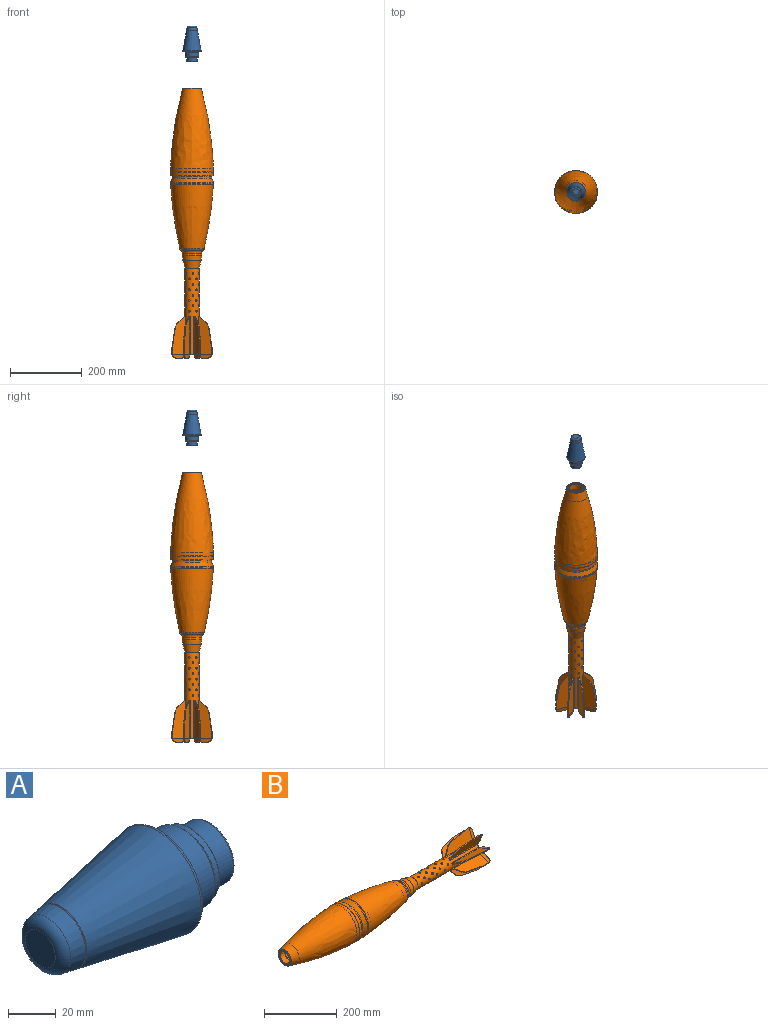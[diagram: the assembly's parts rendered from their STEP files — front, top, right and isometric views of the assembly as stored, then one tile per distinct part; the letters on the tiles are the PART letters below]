
ASSEMBLY  parts=2 mates=1
PART A: 17 faces, bbox 100x50.8x50.8 mm
  f0: torus R=13.88mm, axis (-1,0,0), area 149.5mm2, adj f1,f14
  f1: plane 27.76x27.76mm, normal (1,0,0), area 605.3mm2, adj f0
  f2: plane 17.63x17.63mm, normal (-1,0,0), area 244.1mm2, adj f16
  f3: cone r=13mm half-angle=10.1deg, axis (1,0,0), area 702.8mm2, adj f4,f16
  f4: torus R=15.15mm, axis (-1,0,0), area 74mm2, adj f3,f5
  f5: cone r=15.19mm half-angle=10.1deg, axis (1,0,0), area 7404mm2, adj f4,f6
  f6: cylinder r=25.42mm len=50.83mm, axis (-1,0,0), area 149.7mm2, adj f5,f7
  f7: plane 50.83x50.83mm, normal (1,0,0), area 1044.3mm2, adj f6,f8
  f8: cylinder r=17.71mm len=35.42mm, axis (-1,0,0), area 266.6mm2, adj f7,f9
  f9: cone r=17.71mm half-angle=45deg, axis (1,0,0), area 248.7mm2, adj f8,f10
  f10: cylinder r=19.22mm len=38.45mm, axis (-1,0,0), area 1168.9mm2, adj f9,f11
  f11: cone r=19.22mm half-angle=45deg, axis (-1,0,0), area 248.7mm2, adj f10,f12
  f12: cylinder r=17.71mm len=35.42mm, axis (-1,0,0), area 292.1mm2, adj f11,f15
  f13: plane 34.42x34.42mm, normal (1,0,0), area 230.8mm2, adj f14,f15
  f14: cylinder r=14.92mm len=29.84mm, axis (-1,0,0), area 976.6mm2, adj f0,f13
  f15: cone r=17.71mm half-angle=45deg, axis (-1,0,0), area 77.6mm2, adj f12,f13
  f16: torus R=8.82mm, axis (-1,0,0), area 515.4mm2, adj f2,f3
PART B: 246 faces, bbox 750x124.9x124.9 mm
  f0: plane 119.06x119.06mm, normal (1,0,0), area 70.5mm2, adj f3,f17
  f1: cone r=59.71mm half-angle=19.9deg, axis (1,0,0), area 4983.2mm2, adj f2,f6
  f2: cylinder r=59.71mm len=119.42mm, axis (-1,0,0), area 750.4mm2, adj f1,f3
  f3: revolved ~119.42x119.42mm, area 1125.9mm2, adj f0,f2
  f4: cylinder r=59.71mm len=119.42mm, axis (-1,0,0), area 3376.6mm2, adj f8,f9
  f5: plane 118.42x118.42mm, normal (1,0,0), area 1162.6mm2, adj f7,f9
  f6: cylinder r=55mm len=110mm, axis (-1,0,0), area 2073.5mm2, adj f1,f7
  f7: torus R=56mm, axis (-1,0,0), area 546.4mm2, adj f5,f6
  f8: cone r=59.21mm half-angle=45deg, axis (1,0,0), area 264.2mm2, adj f4,f203
  f9: cone r=59.71mm half-angle=45deg, axis (-1,0,0), area 264.2mm2, adj f4,f5
  f10: cone r=20mm half-angle=14deg, axis (-1,0,0), area 3215.5mm2, adj f11,f85
  f11: revolved ~54.46x54.46mm, area 2453.5mm2, adj f10,f12
  f12: cylinder r=27.23mm len=54.46mm, axis (-1,0,0), area 939.4mm2, adj f11,f13
  f13: torus R=37.23mm, axis (-1,0,0), area 1393mm2, adj f12,f14
  f14: cone r=30.16mm half-angle=45deg, axis (-1,0,0), area 331.2mm2, adj f13,f15
  f15: torus R=24.3mm, axis (-1,0,0), area 1161.1mm2, adj f14,f16
  f16: revolved ~176.81x119.04mm, area 55262.1mm2, adj f15,f17
  f17: cone r=59.34mm half-angle=41.5deg, axis (1,0,0), area 99.5mm2, adj f0,f16
  f18: plane 37.6x15.64mm, normal (0.1,0.38,-0.92), area 365.6mm2, adj f84,f86,f87,f88,f89
  f19: plane 37.6x15.64mm, normal (0.1,-0.38,0.92), area 365.6mm2, adj f84,f86,f87,f88,f90
  f20: cylinder r=30mm len=4.98mm, axis (0,0.38,-0.92), area 15mm2, adj f27,f28,f89,f90
  f21: cylinder r=30mm len=18.62mm, axis (0,0.38,-0.92), area 66.5mm2, adj f26,f27,f89,f90
  f22: cylinder r=2mm len=106.15mm, axis (1,0,0), area 298.3mm2, adj f24,f25,f26,f84,f85,f89
  f23: cylinder r=2mm len=106.15mm, axis (1,0,0), area 298.3mm2, adj f24,f25,f26,f84,f85,f90
  f24: plane 5.88x2.45mm, normal (-1,0,0), area 1mm2, adj f22,f23,f25,f85
  f25: plane 4.18x1.73mm, normal (0,0.92,0.38), area 0.7mm2, adj f22,f23,f24,f26
  f26: plane 19.65x15.46mm, normal (-0.79,0.57,0.24), area 76.1mm2, adj f21,f22,f23,f25,f89,f90
  f27: plane 49.44x8.84mm, normal (-0.17,0.91,0.38), area 150.4mm2, adj f20,f21,f89,f90
  f28: plane 17.49x2.77mm, normal (0,0.92,0.38), area 52.5mm2, adj f20,f86,f89,f90
  f29: cylinder r=2.62mm len=11mm, axis (0,-0.61,-0.79), area 158mm2, adj f83,f85
  f30: cylinder r=2.62mm len=11.09mm, axis (0,0.38,-0.92), area 158mm2, adj f83,f85
  f31: cylinder r=2.62mm len=10.44mm, axis (0,0.99,-0.13), area 158mm2, adj f83,f85
  f32: cylinder r=2.62mm len=11mm, axis (0,0.61,0.79), area 158mm2, adj f83,f85
  f33: cylinder r=2.62mm len=10.44mm, axis (0,-0.99,0.13), area 158mm2, adj f83,f85
  f34: cylinder r=2.62mm len=11mm, axis (0,-0.61,-0.79), area 158mm2, adj f83,f85
  f35: cylinder r=2.62mm len=11.09mm, axis (0,0.38,-0.92), area 158mm2, adj f83,f85
  f36: cylinder r=2.62mm len=10.44mm, axis (0,0.99,-0.13), area 158mm2, adj f83,f85
  f37: cylinder r=2.62mm len=11mm, axis (0,0.61,0.79), area 158mm2, adj f83,f85
  f38: cylinder r=2.62mm len=10.44mm, axis (0,-0.99,0.13), area 158mm2, adj f83,f85
  f39: cylinder r=2.62mm len=11mm, axis (0,-0.61,-0.79), area 158mm2, adj f83,f85
  f40: cylinder r=2.62mm len=11.09mm, axis (0,0.38,-0.92), area 158mm2, adj f83,f85
  f41: cylinder r=2.62mm len=10.44mm, axis (0,0.99,-0.13), area 158mm2, adj f83,f85
  f42: cylinder r=2.62mm len=11mm, axis (0,0.61,0.79), area 158mm2, adj f83,f85
  f43: cylinder r=2.62mm len=10.44mm, axis (0,-0.99,0.13), area 158mm2, adj f83,f85
  f44: cylinder r=2.62mm len=11mm, axis (0,-0.61,-0.79), area 158mm2, adj f83,f85
  f45: cylinder r=2.62mm len=11.09mm, axis (0,0.38,-0.92), area 158mm2, adj f83,f85
  f46: cylinder r=2.62mm len=10.44mm, axis (0,0.99,-0.13), area 158mm2, adj f83,f85
  f47: cylinder r=2.62mm len=11mm, axis (0,0.61,0.79), area 158mm2, adj f83,f85
  f48: cylinder r=2.62mm len=10.44mm, axis (0,-0.99,0.13), area 158mm2, adj f83,f85
  f49: cylinder r=2.62mm len=11.09mm, axis (0,-0.38,0.92), area 158mm2, adj f83,f85
  f50: cylinder r=2.62mm len=11.09mm, axis (0,-0.38,0.92), area 158mm2, adj f83,f85
  f51: cylinder r=2.62mm len=11.09mm, axis (0,-0.38,0.92), area 158mm2, adj f83,f85
  f52: cylinder r=2.62mm len=11.09mm, axis (0,-0.38,0.92), area 158mm2, adj f83,f85
  f53: cylinder r=2.62mm len=11mm, axis (0,0.79,-0.61), area 158mm2, adj f83,f85
  f54: cylinder r=2.62mm len=11.09mm, axis (0,0.92,0.38), area 158mm2, adj f83,f85
  f55: cylinder r=2.62mm len=10.44mm, axis (0,0.13,0.99), area 158mm2, adj f83,f85
  f56: cylinder r=2.62mm len=11mm, axis (0,-0.79,0.61), area 158mm2, adj f83,f85
  f57: cylinder r=2.62mm len=10.44mm, axis (0,-0.13,-0.99), area 158mm2, adj f83,f85
  f58: cylinder r=2.62mm len=11mm, axis (0,0.79,-0.61), area 158mm2, adj f83,f85
  f59: cylinder r=2.62mm len=11.09mm, axis (0,0.92,0.38), area 158mm2, adj f83,f85
  f60: cylinder r=2.62mm len=10.44mm, axis (0,0.13,0.99), area 158mm2, adj f83,f85
  f61: cylinder r=2.62mm len=11mm, axis (0,-0.79,0.61), area 158mm2, adj f83,f85
  f62: cylinder r=2.62mm len=10.44mm, axis (0,-0.13,-0.99), area 158mm2, adj f83,f85
  f63: cylinder r=2.62mm len=11mm, axis (0,0.79,-0.61), area 158mm2, adj f83,f85
  f64: cylinder r=2.62mm len=11.09mm, axis (0,0.92,0.38), area 158mm2, adj f83,f85
  f65: cylinder r=2.62mm len=10.44mm, axis (0,0.13,0.99), area 158mm2, adj f83,f85
  f66: cylinder r=2.62mm len=11mm, axis (0,-0.79,0.61), area 158mm2, adj f83,f85
  f67: cylinder r=2.62mm len=10.44mm, axis (0,-0.13,-0.99), area 158mm2, adj f83,f85
  f68: cylinder r=2.62mm len=11mm, axis (0,0.79,-0.61), area 158mm2, adj f83,f85
  f69: cylinder r=2.62mm len=11.09mm, axis (0,0.92,0.38), area 158mm2, adj f83,f85
  f70: cylinder r=2.62mm len=10.44mm, axis (0,0.13,0.99), area 158mm2, adj f83,f85
  f71: cylinder r=2.62mm len=11mm, axis (0,-0.79,0.61), area 158mm2, adj f83,f85
  f72: cylinder r=2.62mm len=10.44mm, axis (0,-0.13,-0.99), area 158mm2, adj f83,f85
  f73: cylinder r=2.62mm len=11.09mm, axis (0,-0.92,-0.38), area 158mm2, adj f83,f85
  f74: cylinder r=2.62mm len=11.09mm, axis (0,-0.92,-0.38), area 158mm2, adj f83,f85
  f75: cylinder r=2.62mm len=11.09mm, axis (0,-0.92,-0.38), area 158mm2, adj f83,f85
  f76: cylinder r=2.62mm len=11.09mm, axis (0,-0.92,-0.38), area 158mm2, adj f83,f85
  f77: plane 28x28mm, normal (1,0,0), area 149.3mm2, adj f78,f82
  f78: cone r=12.19mm half-angle=45deg, axis (1,0,0), area 103.8mm2, adj f77,f79
  f79: cylinder r=11.19mm len=23mm, axis (1,0,0), area 1616.4mm2, adj f78,f80
  f80: plane 22.37x22.37mm, normal (1,0,0), area 46.7mm2, adj f79,f83
  f81: plane 21x21mm, normal (1,0,0), area 346.4mm2, adj f83
  f82: cylinder r=14mm len=28mm, axis (1,0,0), area 263.9mm2, adj f77,f84
  f83: cylinder r=10.5mm len=203mm, axis (1,0,0), area 12346.6mm2, adj f29,f30,f31,f32,f33,f34,f35,f36
  f84: plane 41.29x41.29mm, normal (1,0,0), area 627.3mm2, adj f18,f19,f22,f23,f82,f85,f87,f99
  f85: cylinder r=20mm len=240mm, axis (1,0,0), area 23693.2mm2, adj f10,f22,f23,f24,f29,f30,f31,f32
  f86: cylinder r=10mm len=10.39mm, axis (0,0.38,-0.92), area 27.1mm2, adj f18,f19,f28,f88
  f87: cylinder r=10mm len=10.39mm, axis (0,0.38,-0.92), area 27.1mm2, adj f18,f19,f84,f88
  f88: plane 19.49x8.82mm, normal (1,0,0), area 20.7mm2, adj f18,f19,f86,f87
  f89: plane 104.77x35.08mm, normal (0,0.38,-0.92), area 3101.8mm2, adj f18,f20,f21,f22,f26,f27,f28
  f90: plane 104.77x35.08mm, normal (0,-0.38,0.92), area 3101.8mm2, adj f19,f20,f21,f23,f26,f27,f28
  f91: plane 104.77x35.05mm, normal (0,-0.92,0.38), area 3101.8mm2, adj f96,f97,f98,f100,f103,f104,f106
  f92: plane 104.77x35.05mm, normal (0,0.92,-0.38), area 3101.8mm2, adj f96,f97,f98,f99,f103,f104,f105
  f93: plane 19.48x8.85mm, normal (1,0,0), area 20.7mm2, adj f101,f102,f105,f106
  f94: plane 5.88x2.46mm, normal (-1,0,0), area 1mm2, adj f85,f95,f99,f100
  f95: plane 4.18x1.73mm, normal (0,0.38,0.92), area 0.7mm2, adj f94,f96,f99,f100
  f96: plane 19.65x15.46mm, normal (-0.79,0.24,0.57), area 76.1mm2, adj f91,f92,f95,f99,f100,f103
  f97: plane 49.44x8.84mm, normal (-0.17,0.38,0.91), area 150.4mm2, adj f91,f92,f103,f104
  f98: plane 17.49x2.77mm, normal (0,0.38,0.92), area 52.5mm2, adj f91,f92,f102,f104
  f99: cylinder r=2mm len=106.15mm, axis (1,0,0), area 298.3mm2, adj f84,f85,f92,f94,f95,f96
  f100: cylinder r=2mm len=106.15mm, axis (1,0,0), area 298.3mm2, adj f84,f85,f91,f94,f95,f96
  f101: cylinder r=10mm len=10.39mm, axis (0,0.92,-0.38), area 27.1mm2, adj f84,f93,f105,f106
  f102: cylinder r=10mm len=10.39mm, axis (0,0.92,-0.38), area 27.1mm2, adj f93,f98,f105,f106
  f103: cylinder r=30mm len=18.62mm, axis (0,0.92,-0.38), area 66.5mm2, adj f91,f92,f96,f97
  f104: cylinder r=30mm len=4.98mm, axis (0,0.92,-0.38), area 15mm2, adj f91,f92,f97,f98
  f105: plane 37.57x15.71mm, normal (0.1,0.92,-0.38), area 365.6mm2, adj f84,f92,f93,f101,f102
  f106: plane 37.57x15.71mm, normal (0.1,-0.92,0.38), area 365.6mm2, adj f84,f91,f93,f101,f102
  f107: plane 104.77x35.08mm, normal (0,-0.92,-0.38), area 3101.8mm2, adj f112,f113,f114,f116,f119,f120,f122
  f108: plane 104.77x35.08mm, normal (0,0.92,0.38), area 3101.8mm2, adj f112,f113,f114,f115,f119,f120,f121
  f109: plane 19.49x8.82mm, normal (1,0,0), area 20.7mm2, adj f117,f118,f121,f122
  f110: plane 5.88x2.45mm, normal (-1,0,0), area 1mm2, adj f85,f111,f115,f116
  f111: plane 4.18x1.73mm, normal (0,-0.38,0.92), area 0.7mm2, adj f110,f112,f115,f116
  f112: plane 19.65x15.46mm, normal (-0.79,-0.24,0.57), area 76.1mm2, adj f107,f108,f111,f115,f116,f119
  f113: plane 49.44x8.84mm, normal (-0.17,-0.38,0.91), area 150.4mm2, adj f107,f108,f119,f120
  f114: plane 17.49x2.77mm, normal (0,-0.38,0.92), area 52.5mm2, adj f107,f108,f118,f120
  f115: cylinder r=2mm len=106.15mm, axis (1,0,0), area 298.3mm2, adj f84,f85,f108,f110,f111,f112
  f116: cylinder r=2mm len=106.15mm, axis (1,0,0), area 298.3mm2, adj f84,f85,f107,f110,f111,f112
  f117: cylinder r=10mm len=10.39mm, axis (0,0.92,0.38), area 27.1mm2, adj f84,f109,f121,f122
  f118: cylinder r=10mm len=10.39mm, axis (0,0.92,0.38), area 27.1mm2, adj f109,f114,f121,f122
  f119: cylinder r=30mm len=18.62mm, axis (0,0.92,0.38), area 66.5mm2, adj f107,f108,f112,f113
  f120: cylinder r=30mm len=4.98mm, axis (0,0.92,0.38), area 15mm2, adj f107,f108,f113,f114
  f121: plane 37.6x15.64mm, normal (0.1,0.92,0.38), area 365.6mm2, adj f84,f108,f109,f117,f118
  f122: plane 37.6x15.64mm, normal (0.1,-0.92,-0.38), area 365.6mm2, adj f84,f107,f109,f117,f118
  f123: plane 104.77x35.05mm, normal (0,-0.38,-0.92), area 3101.8mm2, adj f128,f129,f130,f132,f135,f136,f138
  f124: plane 104.77x35.05mm, normal (0,0.38,0.92), area 3101.8mm2, adj f128,f129,f130,f131,f135,f136,f137
  f125: plane 19.48x8.85mm, normal (1,0,0), area 20.7mm2, adj f133,f134,f137,f138
  f126: plane 5.88x2.46mm, normal (-1,0,0), area 1mm2, adj f85,f127,f131,f132
  f127: plane 4.18x1.73mm, normal (0,-0.92,0.38), area 0.7mm2, adj f126,f128,f131,f132
  f128: plane 19.65x15.46mm, normal (-0.79,-0.57,0.24), area 76.1mm2, adj f123,f124,f127,f131,f132,f135
  f129: plane 49.44x8.84mm, normal (-0.17,-0.91,0.38), area 150.4mm2, adj f123,f124,f135,f136
  f130: plane 17.49x2.77mm, normal (0,-0.92,0.38), area 52.5mm2, adj f123,f124,f134,f136
  f131: cylinder r=2mm len=106.15mm, axis (1,0,0), area 298.3mm2, adj f84,f85,f124,f126,f127,f128
  f132: cylinder r=2mm len=106.15mm, axis (1,0,0), area 298.3mm2, adj f84,f85,f123,f126,f127,f128
  f133: cylinder r=10mm len=10.39mm, axis (0,0.38,0.92), area 27.1mm2, adj f84,f125,f137,f138
  f134: cylinder r=10mm len=10.39mm, axis (0,0.38,0.92), area 27.1mm2, adj f125,f130,f137,f138
  f135: cylinder r=30mm len=18.62mm, axis (0,0.38,0.92), area 66.5mm2, adj f123,f124,f128,f129
  f136: cylinder r=30mm len=4.98mm, axis (0,0.38,0.92), area 15mm2, adj f123,f124,f129,f130
  f137: plane 37.57x15.71mm, normal (0.1,0.38,0.92), area 365.6mm2, adj f84,f124,f125,f133,f134
  f138: plane 37.57x15.71mm, normal (0.1,-0.38,-0.92), area 365.6mm2, adj f84,f123,f125,f133,f134
  f139: plane 104.77x35.08mm, normal (0,0.38,-0.92), area 3101.8mm2, adj f144,f145,f146,f148,f151,f152,f154
  f140: plane 104.77x35.08mm, normal (0,-0.38,0.92), area 3101.8mm2, adj f144,f145,f146,f147,f151,f152,f153
  f141: plane 19.49x8.82mm, normal (1,0,0), area 20.7mm2, adj f149,f150,f153,f154
  f142: plane 5.88x2.45mm, normal (-1,0,0), area 1mm2, adj f85,f143,f147,f148
  f143: plane 4.18x1.73mm, normal (0,-0.92,-0.38), area 0.7mm2, adj f142,f144,f147,f148
  f144: plane 19.65x15.46mm, normal (-0.79,-0.57,-0.24), area 76.1mm2, adj f139,f140,f143,f147,f148,f151
  f145: plane 49.44x8.84mm, normal (-0.17,-0.91,-0.38), area 150.4mm2, adj f139,f140,f151,f152
  f146: plane 17.49x2.77mm, normal (0,-0.92,-0.38), area 52.5mm2, adj f139,f140,f150,f152
  f147: cylinder r=2mm len=106.15mm, axis (1,0,0), area 298.3mm2, adj f84,f85,f140,f142,f143,f144
  f148: cylinder r=2mm len=106.15mm, axis (1,0,0), area 298.3mm2, adj f84,f85,f139,f142,f143,f144
  f149: cylinder r=10mm len=10.39mm, axis (0,-0.38,0.92), area 27.1mm2, adj f84,f141,f153,f154
  f150: cylinder r=10mm len=10.39mm, axis (0,-0.38,0.92), area 27.1mm2, adj f141,f146,f153,f154
  f151: cylinder r=30mm len=18.62mm, axis (0,-0.38,0.92), area 66.5mm2, adj f139,f140,f144,f145
  f152: cylinder r=30mm len=4.98mm, axis (0,-0.38,0.92), area 15mm2, adj f139,f140,f145,f146
  f153: plane 37.6x15.64mm, normal (0.1,-0.38,0.92), area 365.6mm2, adj f84,f140,f141,f149,f150
  f154: plane 37.6x15.64mm, normal (0.1,0.38,-0.92), area 365.6mm2, adj f84,f139,f141,f149,f150
  f155: plane 104.77x35.05mm, normal (0,0.92,-0.38), area 3101.8mm2, adj f160,f161,f162,f164,f167,f168,f170
  f156: plane 104.77x35.05mm, normal (0,-0.92,0.38), area 3101.8mm2, adj f160,f161,f162,f163,f167,f168,f169
  f157: plane 19.48x8.85mm, normal (1,0,0), area 20.7mm2, adj f165,f166,f169,f170
  f158: plane 5.88x2.46mm, normal (-1,0,0), area 1mm2, adj f85,f159,f163,f164
  f159: plane 4.18x1.73mm, normal (0,-0.38,-0.92), area 0.7mm2, adj f158,f160,f163,f164
  f160: plane 19.65x15.46mm, normal (-0.79,-0.24,-0.57), area 76.1mm2, adj f155,f156,f159,f163,f164,f167
  f161: plane 49.44x8.84mm, normal (-0.17,-0.38,-0.91), area 150.4mm2, adj f155,f156,f167,f168
  f162: plane 17.49x2.77mm, normal (0,-0.38,-0.92), area 52.5mm2, adj f155,f156,f166,f168
  f163: cylinder r=2mm len=106.15mm, axis (1,0,0), area 298.3mm2, adj f84,f85,f156,f158,f159,f160
  f164: cylinder r=2mm len=106.15mm, axis (1,0,0), area 298.3mm2, adj f84,f85,f155,f158,f159,f160
  f165: cylinder r=10mm len=10.39mm, axis (0,-0.92,0.38), area 27.1mm2, adj f84,f157,f169,f170
  f166: cylinder r=10mm len=10.39mm, axis (0,-0.92,0.38), area 27.1mm2, adj f157,f162,f169,f170
  f167: cylinder r=30mm len=18.62mm, axis (0,-0.92,0.38), area 66.5mm2, adj f155,f156,f160,f161
  f168: cylinder r=30mm len=4.98mm, axis (0,-0.92,0.38), area 15mm2, adj f155,f156,f161,f162
  f169: plane 37.57x15.71mm, normal (0.1,-0.92,0.38), area 365.6mm2, adj f84,f156,f157,f165,f166
  f170: plane 37.57x15.71mm, normal (0.1,0.92,-0.38), area 365.6mm2, adj f84,f155,f157,f165,f166
  f171: plane 104.77x35.08mm, normal (0,0.92,0.38), area 3101.8mm2, adj f176,f177,f178,f180,f183,f184,f186
  f172: plane 104.77x35.08mm, normal (0,-0.92,-0.38), area 3101.8mm2, adj f176,f177,f178,f179,f183,f184,f185
  f173: plane 19.49x8.82mm, normal (1,0,0), area 20.7mm2, adj f181,f182,f185,f186
  f174: plane 5.88x2.45mm, normal (-1,0,0), area 1mm2, adj f85,f175,f179,f180
  f175: plane 4.18x1.73mm, normal (0,0.38,-0.92), area 0.7mm2, adj f174,f176,f179,f180
  f176: plane 19.65x15.46mm, normal (-0.79,0.24,-0.57), area 76.1mm2, adj f171,f172,f175,f179,f180,f183
  f177: plane 49.44x8.84mm, normal (-0.17,0.38,-0.91), area 150.4mm2, adj f171,f172,f183,f184
  f178: plane 17.49x2.77mm, normal (0,0.38,-0.92), area 52.5mm2, adj f171,f172,f182,f184
  f179: cylinder r=2mm len=106.15mm, axis (1,0,0), area 298.3mm2, adj f84,f85,f172,f174,f175,f176
  f180: cylinder r=2mm len=106.15mm, axis (1,0,0), area 298.3mm2, adj f84,f85,f171,f174,f175,f176
  f181: cylinder r=10mm len=10.39mm, axis (0,-0.92,-0.38), area 27.1mm2, adj f84,f173,f185,f186
  f182: cylinder r=10mm len=10.39mm, axis (0,-0.92,-0.38), area 27.1mm2, adj f173,f178,f185,f186
  f183: cylinder r=30mm len=18.62mm, axis (0,-0.92,-0.38), area 66.5mm2, adj f171,f172,f176,f177
  f184: cylinder r=30mm len=4.98mm, axis (0,-0.92,-0.38), area 15mm2, adj f171,f172,f177,f178
  f185: plane 37.6x15.64mm, normal (0.1,-0.92,-0.38), area 365.6mm2, adj f84,f172,f173,f181,f182
  f186: plane 37.6x15.64mm, normal (0.1,0.92,0.38), area 365.6mm2, adj f84,f171,f173,f181,f182
  f187: plane 104.77x35.05mm, normal (0,0.38,0.92), area 3101.8mm2, adj f192,f193,f194,f196,f199,f200,f202
  f188: plane 104.77x35.05mm, normal (0,-0.38,-0.92), area 3101.8mm2, adj f192,f193,f194,f195,f199,f200,f201
  f189: plane 19.48x8.85mm, normal (1,0,0), area 20.7mm2, adj f197,f198,f201,f202
  f190: plane 5.88x2.46mm, normal (-1,0,0), area 1mm2, adj f85,f191,f195,f196
  f191: plane 4.18x1.73mm, normal (0,0.92,-0.38), area 0.7mm2, adj f190,f192,f195,f196
  f192: plane 19.65x15.46mm, normal (-0.79,0.57,-0.24), area 76.1mm2, adj f187,f188,f191,f195,f196,f199
  f193: plane 49.44x8.84mm, normal (-0.17,0.91,-0.38), area 150.4mm2, adj f187,f188,f199,f200
  f194: plane 17.49x2.77mm, normal (0,0.92,-0.38), area 52.5mm2, adj f187,f188,f198,f200
  f195: cylinder r=2mm len=106.15mm, axis (1,0,0), area 298.3mm2, adj f84,f85,f188,f190,f191,f192
  f196: cylinder r=2mm len=106.15mm, axis (1,0,0), area 298.3mm2, adj f84,f85,f187,f190,f191,f192
  f197: cylinder r=10mm len=10.39mm, axis (0,-0.38,-0.92), area 27.1mm2, adj f84,f189,f201,f202
  f198: cylinder r=10mm len=10.39mm, axis (0,-0.38,-0.92), area 27.1mm2, adj f189,f194,f201,f202
  f199: cylinder r=30mm len=18.62mm, axis (0,-0.38,-0.92), area 66.5mm2, adj f187,f188,f192,f193
  f200: cylinder r=30mm len=4.98mm, axis (0,-0.38,-0.92), area 15mm2, adj f187,f188,f193,f194
  f201: plane 37.57x15.71mm, normal (0.1,-0.38,-0.92), area 365.6mm2, adj f84,f188,f189,f197,f198
  f202: plane 37.57x15.71mm, normal (0.1,0.38,0.92), area 365.6mm2, adj f84,f187,f189,f197,f198
  f203: cone r=59.71mm half-angle=45deg, axis (-1,0,0), area 264.2mm2, adj f8,f209
  f204: cone r=23.35mm half-angle=60.5deg, axis (1,0,0), area 454.4mm2, adj f207,f208
  f205: cylinder r=18.36mm len=36.73mm, axis (-1,0,0), area 2020.8mm2, adj f206,f213
  f206: cone r=20.36mm half-angle=45deg, axis (-1,0,0), area 344.1mm2, adj f205,f207
  f207: plane 46.71x46.71mm, normal (-1,0,0), area 410.9mm2, adj f204,f206
  f208: revolved ~221.56x119.42mm, area 66588.3mm2, adj f204,f209
  f209: cylinder r=59.71mm len=119.42mm, axis (-1,0,0), area 3564.2mm2, adj f203,f208
  f210: revolved ~195.58x115.41mm, area 59102.4mm2, adj f211,f214
  f211: torus R=27.69mm, axis (-1,0,0), area 736.5mm2, adj f210,f212
  f212: plane 55.37x55.37mm, normal (1,0,0), area 621.4mm2, adj f211,f213
  f213: cone r=18.36mm half-angle=45deg, axis (1,0,0), area 1028.7mm2, adj f205,f212
  f214: torus R=47.71mm, axis (-1,0,0), area 48.8mm2, adj f210,f226
  f215: plane 24x24mm, normal (-1,0,0), area 452.4mm2, adj f216
  f216: torus R=12mm, axis (-1,0,0), area 60.8mm2, adj f215,f217
  f217: cylinder r=12.5mm len=25mm, axis (1,0,0), area 233.1mm2, adj f216,f218
  f218: cone r=12.5mm half-angle=26.8deg, axis (-1,0,0), area 84.9mm2, adj f217,f219
  f219: torus R=4.69mm, axis (-1,0,0), area 3486.9mm2, adj f218,f220
  f220: torus R=29.92mm, axis (-1,0,0), area 244.8mm2, adj f219,f221
  f221: plane 67.29x67.29mm, normal (-1,0,0), area 743.7mm2, adj f220,f222
  f222: torus R=33.64mm, axis (-1,0,0), area 595.4mm2, adj f221,f223
  f223: revolved ~150.68x113.73mm, area 45907.1mm2, adj f222,f224
  f224: plane 113.73x113.73mm, normal (1,0,0), area 2035.5mm2, adj f223,f225
  f225: cone r=51.71mm half-angle=0.9deg, axis (-1,0,0), area 17722.6mm2, adj f224,f226
  f226: plane 115.42x115.42mm, normal (-1,0,0), area 2063.3mm2, adj f214,f225
  f227: plane 116.42x116.42mm, normal (-1,0,0), area 182.1mm2, adj f228,f229
  f228: cylinder r=57.71mm len=115.42mm, axis (-1,0,0), area 181.3mm2, adj f227,f229
  f229: cone r=58.21mm half-angle=45deg, axis (1,0,0), area 257.5mm2, adj f227,f228
  f230: revolved ~115.05x115.05mm, area 77.2mm2, adj f231,f232
  f231: plane 115.45x115.45mm, normal (1,0,0), area 72.4mm2, adj f230,f232
  f232: cone r=57.51mm half-angle=45deg, axis (-1,0,0), area 109.2mm2, adj f230,f231
  f233: plane 31x31mm, normal (-1,0,0), area 223.8mm2, adj f234,f235
  f234: cylinder r=13mm len=26mm, axis (1,0,0), area 163.4mm2, adj f233,f236
  f235: cylinder r=15.5mm len=31mm, axis (-1,0,0), area 194.8mm2, adj f233,f236
  f236: plane 31x31mm, normal (1,0,0), area 223.8mm2, adj f234,f235
  f237: cone r=15.5mm half-angle=45deg, axis (1,0,0), area 216.6mm2, adj f238,f239
  f238: cylinder r=15.5mm len=31mm, axis (1,0,0), area 146.1mm2, adj f237,f239
  f239: plane 34x34mm, normal (-1,0,0), area 153.2mm2, adj f237,f238
  f240: cone r=11.5mm half-angle=45deg, axis (1,0,0), area 108.1mm2, adj f241,f245
  f241: plane 23x23mm, normal (-1,0,0), area 415.5mm2, adj f240
  f242: plane 26.5x26.5mm, normal (1,0,0), area 551.5mm2, adj f243
  f243: cylinder r=13.25mm len=26.5mm, axis (-1,0,0), area 333mm2, adj f242,f244
  f244: plane 26.5x26.5mm, normal (-1,0,0), area 59.7mm2, adj f243,f245
  f245: cylinder r=12.51mm len=25.03mm, axis (-1,0,0), area 1mm2, adj f240,f244
PLACE A rot(axis=(0,1,0),90deg) t=(0,0,343.28)mm
PLACE B rot(axis=(-0.71,0,0.71),180deg) t=(0,0,240)mm
MATE slider A.f0 <-> B.f1  axis (0,0,1) through (0,0,834.53)mm
